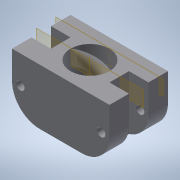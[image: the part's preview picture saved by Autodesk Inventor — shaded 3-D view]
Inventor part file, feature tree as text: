
AUTODESK INVENTOR PART (.ipt)
format: ipt  version: 2020.1 (Build 241239000, 239)  size: 290,304 bytes
history: native  units: mm
features: sketch x5, extrude x4, plane x2, fillet x2, pattern_circular x1, other x1, helix x1
ambient origin geometry x8: Origin, YZ Plane, XZ Plane, XY Plane, X Axis, Y Axis, Z Axis, Center Point
bodies: Solid1 (feature_tree)
feature tree (16):
  extrude  "Extrusion1"  Depth=13.0mm
  extrude  "Extrusion6"  Depth=7.0mm
  extrude  "Extrusion7"  Depth=7.0mm
  pattern_circular  "Circular Pattern3"  [2 undecoded]
  plane  "Work Plane3"
  sketch  "Sketch10"  dims[d59=7.0mm]
  other  "Work Axis1"
  helix  "Coil1"  [1 undecoded]
  fillet  "Fillet4"  Radius=7.0mm
  fillet  "Fillet5"  Radius=7.0mm
  extrude  "Extrusion8"  TaperAngle=90.0deg  [1 undecoded]
  sketch  "Sketch1"  dims[d28=20.0mm d29=0.0mm d49=13.0mm]
  sketch  "Sketch6"  dims[d55=7.0mm d56=7.0mm]
  sketch  "Sketch7"  dims[d57=7.0mm d58=7.0mm]
  plane  "Work Plane2"
  sketch  "Sketch11"  dims[d60=7.0mm d61=7.0mm d62=90.0deg d63=7.0mm d64=7.0mm d65=90.0deg d66=7.0mm d67=7.0mm d68=7.0mm d69=7.0mm d70=7.0mm d71=7.0mm d72=7.0mm d73=7.0mm d74=7.0mm d75=7.0mm d76=7.0mm d77=90.0deg d78=13.0mm d81=10.0mm d82=0.0mm d83=3.0mm d84=3.0mm d85=10.0mm d86=0.0mm d87=40.0mm d88=360.0deg d93=7.0mm d94=14.0mm d95=7.0mm d100=2.5mm d101=5.0mm d102=25.0mm d103=15.0mm d104=10.0mm d105=0.0mm d106=90.0deg d107=90.0deg d108=0.0mm d109=0.0mm d111=2.0mm d112=10.0mm d113=10.0mm d114=0.0mm]
note: 4 required parameter values undecoded (feature->parameter linkage not recoverable at this tier; creation-order binding heuristic only, values carry confidence <= 0.55)
